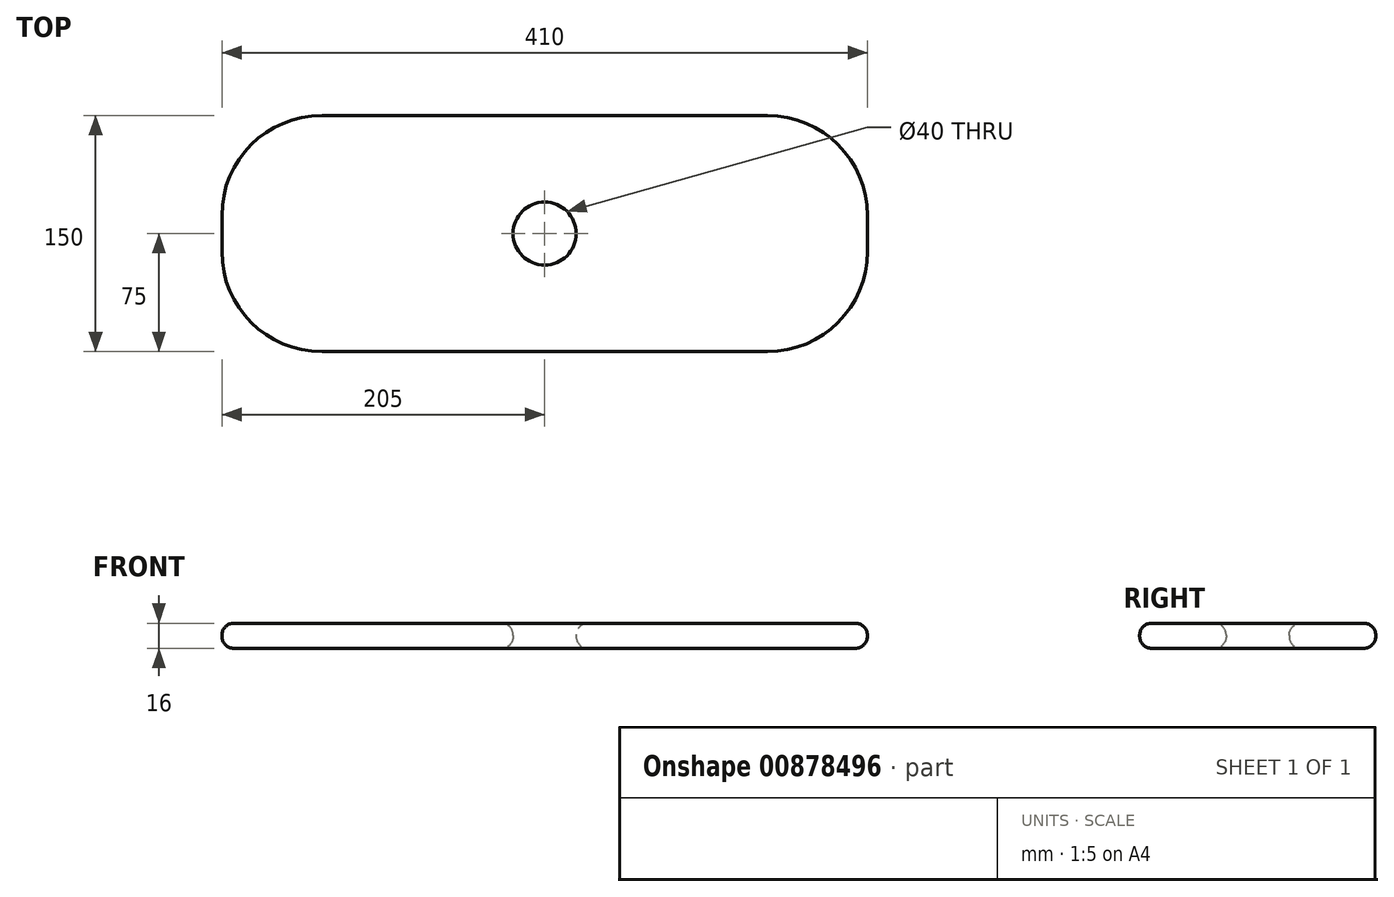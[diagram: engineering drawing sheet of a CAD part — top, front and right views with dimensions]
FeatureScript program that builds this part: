
annotation { "Feature Type Name" : "Feature", "Feature Type Description" : "" }
export const myFeature = defineFeature(function(context is Context, id is Id, definition is map)
    precondition{}
    {
        {
            var Q0;
            Q0=qCreatedBy(makeId("Top.planeOp"),FACE);
            var sketch = newSketch(context, id + "F0", { "sketchPlane" : qUnion([Q0])});
            skLineSegment(sketch, "E0.bottom", {"start": v(0, 0) * mm, "end": v(-410, 0) * mm});
            skLineSegment(sketch, "E0.top", {"start": v(0, 150) * mm, "end": v(-410, 150) * mm});
            skLineSegment(sketch, "E0.left", {"start": v(0, 0) * mm, "end": v(0, 150) * mm});
            skLineSegment(sketch, "E0.right", {"start": v(-410, 0) * mm, "end": v(-410, 150) * mm});
            skSolve(sketch);
        }
        {
            var Q0;
            Q0=makeQuery(id+"F0.imprint","IMPRINT",FACE,{"disambiguationData":[TD([[makeQuery(id+"F0.imprint","IMPRINT",EDGE,{"derivedFrom":sQuery(id+"F0.wireOp",EDGE,"E0.bottom")}),-1.0]])]});
            var Q1;
            Q1 = qSketchRegion(id + "F2", true);
            extrude(context, id + "F1", {"entities" : qUnion([Q0, Q1]), "depth" : 16 * mm, "offsetDistance" : 25.4 * mm});
        }
        {
            var Q0;
            Q0=makeQuery(id+"F1.opExtrude","CAP_FACE",FACE,{"disambiguationData":[OSD([sQuery(id+"F0.wireOp",EDGE,"E0.bottom"),sQuery(id+"F0.wireOp",EDGE,"E0.top"),sQuery(id+"F0.wireOp",EDGE,"E0.left"),sQuery(id+"F0.wireOp",EDGE,"E0.right")])],"isStart":true});
            var sketch = newSketch(context, id + "F2", { "sketchPlane" : qUnion([Q0])});
            skCircle(sketch, "E1", {"center": v(-205, -75) * mm, "radius": 20 * mm});
            skSolve(sketch);
        }
        {
            var Q0;
            Q0=makeQuery(id+"F2.imprint","IMPRINT",FACE,{"disambiguationData":[TD([[makeQuery(id+"F2.imprint","IMPRINT",EDGE,{"derivedFrom":sQuery(id+"F2.wireOp",EDGE,"E1")}),1.0]])]});
            extrude(context, id + "F3", {"entities" : qUnion([Q0]), "operationType" : NewBodyOperationType.REMOVE, "endBound" : BoundingType.THROUGH_ALL, "oppositeDirection" : true, "depth" : 25.4 * mm, "offsetDistance" : 25.4 * mm});
        }
        {
            var Q0;
            Q0=makeQuery(id+"F1.opExtrude","SWEPT_EDGE",EDGE,{"disambiguationData":[OSD([sQuery(id+"F0.wireOp",EDGE,"E0.top"),sQuery(id+"F0.wireOp",EDGE,"E0.right")])]});
            var Q1;
            Q1=makeQuery(id+"F1.opExtrude","SWEPT_EDGE",EDGE,{"disambiguationData":[OSD([sQuery(id+"F0.wireOp",EDGE,"E0.bottom"),sQuery(id+"F0.wireOp",EDGE,"E0.right")])]});
            var Q2;
            Q2=makeQuery(id+"F1.opExtrude","SWEPT_EDGE",EDGE,{"disambiguationData":[OSD([sQuery(id+"F0.wireOp",EDGE,"E0.bottom"),sQuery(id+"F0.wireOp",EDGE,"E0.left")])]});
            var Q3;
            Q3=makeQuery(id+"F1.opExtrude","SWEPT_EDGE",EDGE,{"disambiguationData":[OSD([sQuery(id+"F0.wireOp",EDGE,"E0.top"),sQuery(id+"F0.wireOp",EDGE,"E0.left")])]});
            fillet(context, id + "F4", {"entities" : qUnion([Q0, Q1, Q2, Q3]), "radius" : 63.5 * mm, "tangentPropagation" : true, "allowEdgeOverflow" : false});
        }
        {
            var Q0;
            Q0=makeQuery(id+"F1.opExtrude","CAP_EDGE",EDGE,{"disambiguationData":[OSD([sQuery(id+"F0.wireOp",EDGE,"E0.bottom")])],"isStart":true});
            var Q1;
            Q1=makeQuery(id+"F1.opExtrude","CAP_EDGE",EDGE,{"disambiguationData":[OSD([sQuery(id+"F0.wireOp",EDGE,"E0.bottom")])],"isStart":false});
            var Q2;
            Q2=makeQuery(id+"F3.boolean.opBoolean","INTERSECT",EDGE,{"derivedFrom":[makeQuery(id+"F1.opExtrude","CAP_FACE",FACE,{"disambiguationData":[OSD([sQuery(id+"F0.wireOp",EDGE,"E0.bottom"),sQuery(id+"F0.wireOp",EDGE,"E0.top"),sQuery(id+"F0.wireOp",EDGE,"E0.left"),sQuery(id+"F0.wireOp",EDGE,"E0.right")])],"isStart":false}),makeQuery(id+"F3.opExtrude","SWEPT_FACE",FACE,{"disambiguationData":[OSD([sQuery(id+"F2.wireOp",EDGE,"E1")])]})]});
            var Q3;
            Q3=makeQuery(id+"F1.opExtrude","CAP_FACE",FACE,{"disambiguationData":[OSD([sQuery(id+"F0.wireOp",EDGE,"E0.bottom"),sQuery(id+"F0.wireOp",EDGE,"E0.top"),sQuery(id+"F0.wireOp",EDGE,"E0.left"),sQuery(id+"F0.wireOp",EDGE,"E0.right")])],"isStart":true});
            fillet(context, id + "F5", {"entities" : qUnion([Q0, Q1, Q2, Q3]), "radius" : 7.62 * mm, "tangentPropagation" : true, "allowEdgeOverflow" : false});
        }
    });
